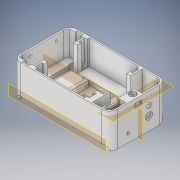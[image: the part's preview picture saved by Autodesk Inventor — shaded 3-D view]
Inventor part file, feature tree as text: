
AUTODESK INVENTOR PART (.ipt)
format: ipt  version: 2019.3 (Build 233278000, 278)  size: 805,888 bytes
history: native  units: mm
features: extrude x21, sketch x21, projected_geometry x13, plane x5, fillet x3, hole x3, mirror x2, chamfer x1
ambient origin geometry x8: Origin, YZ Plane, XZ Plane, XY Plane, X Axis, Y Axis, Z Axis, Center Point
bodies: Solid1 (feature_tree)
feature tree (69):
  extrude  "Extrusion1"  Depth=74.0mm
  extrude  "Extrusion2"  Depth=11.0mm
  extrude  "Extrusion6"  Depth=31.5mm
  extrude  "Extrusion4"  Depth=16.0mm
  plane  "Work Plane2"
  extrude  "Extrusion10"  Depth=7.0mm TaperAngle=0.0deg
  fillet  "Fillet2"  Radius=10.0mm
  extrude  "Extrusion14"  Depth=5.0mm
  extrude  "Extrusion16"  Depth=4.75mm
  extrude  "Extrusion17"  Depth=4.75mm
  plane  "Work Plane4"
  extrude  "Extrusion19"  Depth=14.0mm TaperAngle=0.0deg
  extrude  "Extrusion18"  Depth=10.0mm TaperAngle=0.0deg
  fillet  "Fillet4"  Radius=10.0mm
  mirror  "Mirror4"
  extrude  "Extrusion20"  Depth=2.0mm
  chamfer  "Chamfer2"  Distance=3.0mm
  fillet  "Fillet5"  Radius=2.0mm
  extrude  "Extrusion21"  Depth=17.0mm
  hole  "Hole3"  [1 undecoded]
  hole  "Hole4"  [1 undecoded]
  extrude  "Extrusion22"  Depth=3.0mm
  extrude  "Extrusion23"  Depth=14.0mm TaperAngle=0.0deg
  extrude  "Extrusion26"  Depth=14.0mm
  extrude  "Extrusion27"  Depth=7.0mm
  hole  "Hole5"  [1 undecoded]
  extrude  "Extrusion28"  Depth=14.0mm
  plane  "Work Plane5"
  extrude  "Extrusion29"  Depth=14.0mm
  extrude  "Extrusion30"  Depth=5.0mm
  plane  "Work Plane7"
  extrude  "Extrusion31"  Depth=5.0mm
  mirror  "Mirror5"
  extrude  "Extrusion32"  Depth=14.0mm
  sketch  "Sketch1"  dims[d0=125.0mm d1=74.0mm]
  sketch  "Sketch2"  dims[d2=3.0mm d3=0.0mm d8=11.0mm]
  projected_geometry  "Projected Loop1"
  sketch  "Sketch13"  dims[d9=25.0mm d10=31.5mm]
  sketch  "Sketch18"  dims[d16=3.0mm d17=0.0mm d27=16.0mm]
  sketch  "Sketch21"  dims[d29=18.0mm d30=7.0mm d31=0.0mm d40=10.0mm d41=0.0mm]
  sketch  "Sketch22"  dims[d101=10.0mm d102=5.0mm]
  projected_geometry  "Projected Loop11"
  sketch  "Sketch23"  dims[d103=22.0mm d104=4.75mm]
  projected_geometry  "Projected Loop12"
  sketch  "Sketch25"  dims[d105=4.75mm d106=104.0mm]
  sketch  "Sketch27"  dims[d107=10.5mm d108=14.0mm d109=0.0mm]
  projected_geometry  "Projected Loop13"
  projected_geometry  "Projected Loop15"
  sketch  "Sketch28"  dims[d110=50.0mm d140=37.0mm d141=0.0mm d151=10.0mm]
  projected_geometry  "Projected Loop16"
  sketch  "Sketch29"  dims[d159=8.0mm d160=2.0mm]
  projected_geometry  "Projected Loop17"
  sketch  "Sketch30"  dims[d161=2.0mm]
  projected_geometry  "Projected Loop18"
  sketch  "Sketch31"  dims[d162=2.0mm]
  sketch  "Sketch32"  dims[d163=2.0mm]
  projected_geometry  "Projected Loop19"
  projected_geometry  "Projected Loop20"
  sketch  "Sketch33"  dims[d168=23.0mm]
  sketch  "Sketch34"  dims[d169=16.0mm d170=3.0mm d171=0.0mm d173=2.0mm]
  sketch  "Sketch36"  dims[d175=29.0mm d176=0.0mm d179=17.0mm]
  projected_geometry  "Projected Loop21"
  sketch  "Sketch37"  dims[d180=5.0mm d181=5.0mm d182=0.0mm]
  sketch  "Sketch38"  dims[d188=2.0mm d189=3.0mm]
  projected_geometry  "Projected Loop22"
  plane  "Work Plane6"
  sketch  "Sketch40"  dims[d190=4.0mm d191=0.0mm d193=3.0mm]
  sketch  "Sketch41"  dims[d195=7.0mm d196=32.0mm d197=0.0mm d199=3.0mm d200=7.0mm d201=3.0mm d204=16.0mm d205=16.0mm d206=5.0mm d207=5.0mm d208=3.0mm d209=3.0mm d210=6.0mm d212=9.0mm d213=5.0mm d214=3.0mm d215=20.0mm d216=20.0mm d217=6.0mm d218=3.0mm d219=3.0mm d220=9.0mm d221=5.0mm d222=6.0mm d223=64.0mm d224=5.0mm d225=3.0mm d226=3.0mm d227=5.0mm d228=16.0mm d229=9.0mm d232=3.0mm d233=3.0mm d234=16.0mm d235=6.0mm d236=9.0mm d237=64.0mm d238=31.0mm d239=15.0mm d240=10.0mm d241=5.0mm d243=18.0mm d244=16.0mm d247=2.5mm d248=3.0mm d249=31.0mm d250=22.0mm d251=20.0mm d252=6.0mm d253=2.0mm d254=45.0deg d255=2.0mm d257=21.0mm d258=16.75mm d259=9.0mm d260=16.75mm d261=0.0mm d262=2.5mm d263=3.0mm d264=3.75mm d265=6.0mm d266=5.5mm d267=2.0mm d268=90.0deg d269=83.25mm d270=20.594885mm d271=2.5mm d272=3.0mm d273=3.75mm d274=6.0mm d275=5.5mm d276=2.0mm d277=90.0deg d278=83.25mm d279=0.0mm d280=12.0mm d281=2.0mm d282=15.0mm d283=5.0mm d284=3.0mm d285=0.0mm d286=9.0mm d287=10.0mm d288=10.0mm d289=9.0mm d290=2.5mm d291=0.0mm d294=14.0mm d295=5.0mm d298=7.5mm d299=9.0mm d300=5.0mm d301=0.0mm d302=33.25mm d303=2.0mm d304=5.0mm d305=0.0mm d306=12.0mm d307=6.25mm d308=21.0mm d311=2.4mm d312=6.0mm d313=4.0mm d314=2.0mm d315=90.0deg d316=6.0mm d317=0.0mm d318=13.0mm d319=2.5mm d320=3.0mm d321=7.0mm d322=10.0mm d323=10.0mm d324=5.75mm d325=0.0mm d326=-5.0mm d328=10.0mm d330=28.0mm d331=2.0mm d332=0.0mm d336=3.0mm d337=0.0mm d339=5.0mm d340=4.0mm d341=4.0mm d342=7.0mm d343=5.0mm d344=7.0mm d345=5.0mm d346=2.0mm d347=0.0mm d348=9.0mm d349=5.0mm d350=5.0mm d351=22.5mm d352=2.5mm d353=0.0mm d354=2.0mm d355=2.0mm d356=2.0mm d357=14.0mm]
  projected_geometry  "Projected Loop23"
note: 3 required parameter values undecoded (feature->parameter linkage not recoverable at this tier; creation-order binding heuristic only, values carry confidence <= 0.55)
